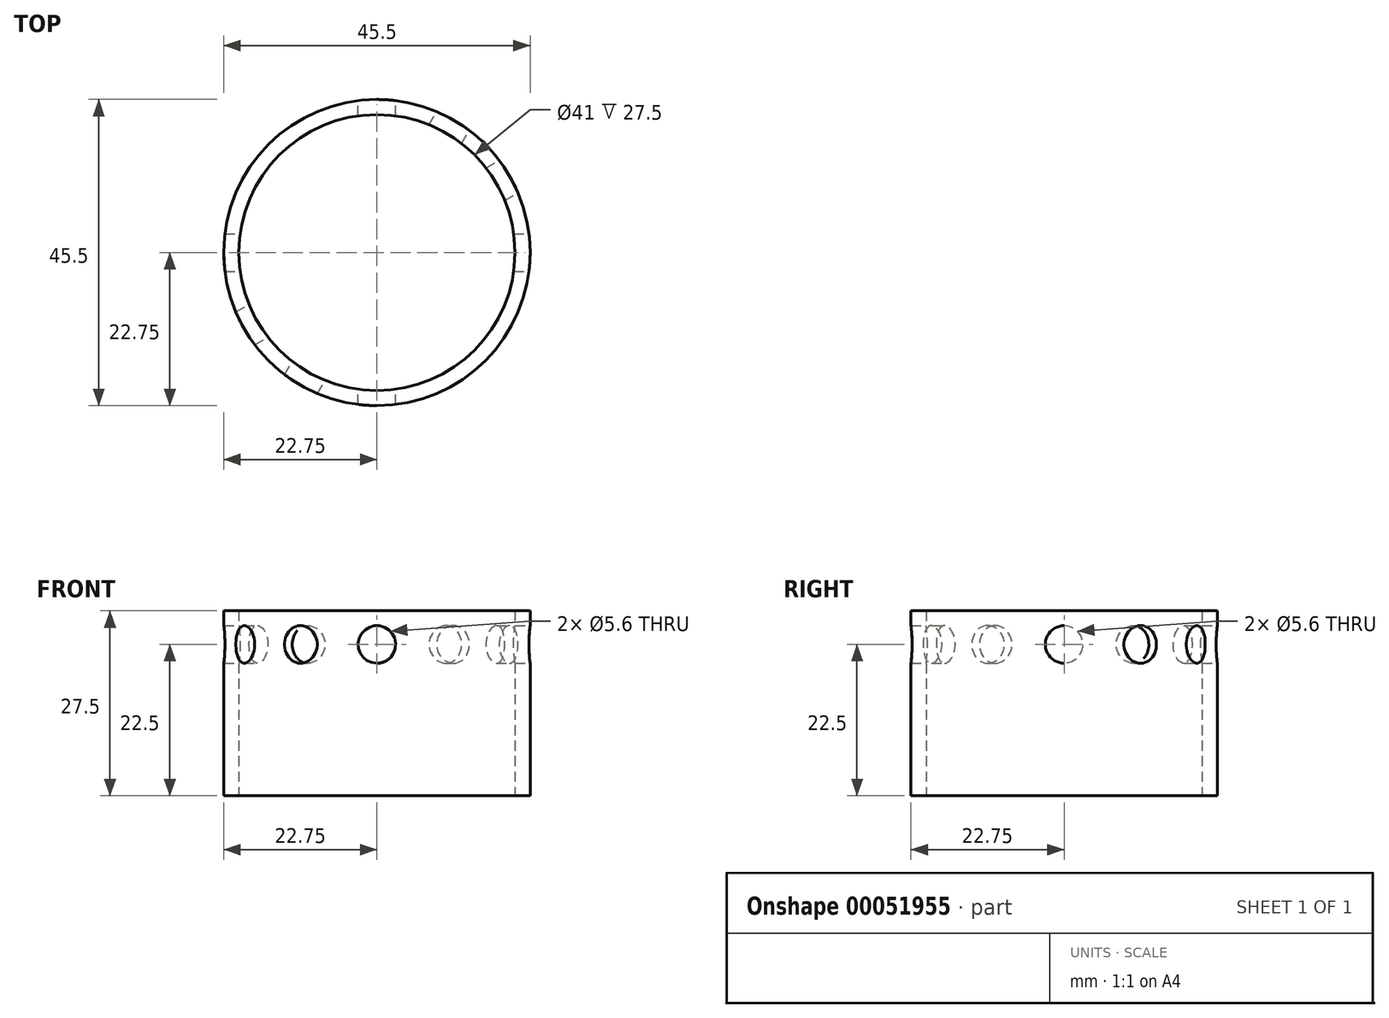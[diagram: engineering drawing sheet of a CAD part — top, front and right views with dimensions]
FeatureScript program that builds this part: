
annotation { "Feature Type Name" : "Feature", "Feature Type Description" : "" }
export const myFeature = defineFeature(function(context is Context, id is Id, definition is map)
    precondition{}
    {
        {
            var Q0;
            Q0=qCreatedBy(makeId("Top.planeOp"),FACE);
            var sketch = newSketch(context, id + "F0", { "sketchPlane" : qUnion([Q0])});
            skCircle(sketch, "E0", {"center": v(0, 0) * mm, "radius": 22.75 * mm});
            skCircle(sketch, "E1", {"center": v(0, 0) * mm, "radius": 20.5 * mm});
            skSolve(sketch);
        }
        {
            var Q0;
            Q0=makeQuery(id+"F0.imprint","IMPRINT",FACE,{"disambiguationData":[TD([[makeQuery(id+"F0.imprint","IMPRINT",EDGE,{"derivedFrom":sQuery(id+"F0.wireOp",EDGE,"E0")}),1.0]])]});
            extrude(context, id + "F1", {"entities" : qUnion([Q0]), "depth" : 27.5 * mm});
        }
        {
            var Q0;
            Q0=qCreatedBy(makeId("Right.planeOp"),FACE);
            var sketch = newSketch(context, id + "F2", { "sketchPlane" : qUnion([Q0])});
            skCircle(sketch, "E2", {"center": v(0, 22.5) * mm, "radius": 2.8 * mm});
            skSolve(sketch);
        }
        {
            var Q0;
            Q0=makeQuery(id+"F2.imprint","IMPRINT",FACE,{"disambiguationData":[TD([[makeQuery(id+"F2.imprint","IMPRINT",EDGE,{"derivedFrom":sQuery(id+"F2.wireOp",EDGE,"E2")}),1.0]])]});
            extrude(context, id + "F3", {"entities" : qUnion([Q0]), "endBound" : BoundingType.SYMMETRIC, "oppositeDirection" : true, "depth" : 50 * mm});
        }
        {
            var Q0;
            Q0=makeQuery(id+"F3.opExtrude","SWEPT_BODY",BODY,{"disambiguationData":[OSD([sQuery(id+"F2.wireOp",EDGE,"E2")])]});
            var Q1;
            Q1=makeQuery(id+"F1.opExtrude","CAP_EDGE",EDGE,{"disambiguationData":[OSD([sQuery(id+"F0.wireOp",EDGE,"E0")])],"isStart":true});
            circularPattern(context, id + "F4", {"entities" : qUnion([Q0]), "axis" : qUnion([Q1]), "angle" : 30 * degree, "instanceCount" : 4});
        }
        {
            var Q0;
            Q0=makeQuery(id+"F4.opPattern","COPY",BODY,{"derivedFrom":makeQuery(id+"F3.opExtrude","SWEPT_BODY",BODY,{"disambiguationData":[OSD([sQuery(id+"F2.wireOp",EDGE,"E2")])]}),"instanceName":"3"});
            var Q1;
            Q1=makeQuery(id+"F4.opPattern","COPY",BODY,{"derivedFrom":makeQuery(id+"F3.opExtrude","SWEPT_BODY",BODY,{"disambiguationData":[OSD([sQuery(id+"F2.wireOp",EDGE,"E2")])]}),"instanceName":"2"});
            var Q2;
            Q2=makeQuery(id+"F4.opPattern","COPY",BODY,{"derivedFrom":makeQuery(id+"F3.opExtrude","SWEPT_BODY",BODY,{"disambiguationData":[OSD([sQuery(id+"F2.wireOp",EDGE,"E2")])]}),"instanceName":"1"});
            var Q3;
            Q3=makeQuery(id+"F3.opExtrude","SWEPT_BODY",BODY,{"disambiguationData":[OSD([sQuery(id+"F2.wireOp",EDGE,"E2")])]});
            var Q4;
            Q4=makeQuery(id+"F1.opExtrude","SWEPT_BODY",BODY,{"disambiguationData":[OSD([sQuery(id+"F0.wireOp",EDGE,"E0"),sQuery(id+"F0.wireOp",EDGE,"E1")])]});
            booleanBodies(context, id + "F5", {"operationType" : BooleanOperationType.SUBTRACTION, "tools" : qUnion([Q0, Q1, Q2, Q3]), "targets" : qUnion([Q4])});
        }
    });
